# Revit family: HL_Вентиляционный клапан_HL900N
name_source: partatom
category: Příslušenství trubek
revit_build: Autodesk Revit 2016 (Build: 20161004_0715(x64)
units: mm (PartAtom-declared; Revit-internal decimal feet)

## family parameters
Kóta kulaté spojky = Použít průměr
Nadpis OmniClass = Liquid Waste Collection and Removal
Ořezat dutým tvarem při načtení = Ne
Sdílené = Ne
Typ součásti = Ventil – zalomení do
Vždy vertikální = Ano
Založené na pracovní rovině = Ne
Číslo OmniClass = 23.70.50.21

## types (1)
- HL_Вентиляционный клапан_HL900N
    Cena = 0 $
    EAN = 9003076909001
    Klíčová poznámka = HL900N
    Komentáře k typům = Вентиляционный клапан DN110 с вдвойне изолированной стеной и с уменьшителем DN50/75
    Model = HL900N
    Popis = Вентиляционный клапан
    URL = http://www.hutterer-lechner.com
    Výrobce = HL Hutterer & Lechner GmbH
    ВЕС = 0,485 kg
    МАТЕРИАЛ = PP
    МАТЕРИАЛ 2 = Plastic - Blue
    ПРОИЗВОДИТЕЛЬНОСТЬ = 37 l/s
    ПРОПУСКНАЯ СПОСОБНОСТЬ = 0.0 m³/h
    РАЗМЕР = DN50/75/110
    материал = Plactic - Gray
